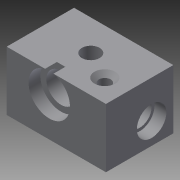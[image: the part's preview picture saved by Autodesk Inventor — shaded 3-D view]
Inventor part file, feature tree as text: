
AUTODESK INVENTOR PART (.ipt)
format: ipt  version: 2015 SP2 (Build 190223200, 223)  size: 123,904 bytes
history: native  units: mm
features: hole x4, sketch x2, extrude x1
ambient origin geometry x8: Origin, YZ Plane, XZ Plane, XY Plane, X Axis, Y Axis, Z Axis, Center Point
bodies: Volumenkörper1 (feature_tree)
feature tree (7):
  extrude  "Extrusion1"  Depth=10.0mm
  hole  "Drill01"  [1 undecoded]
  hole  "Drill02"  [1 undecoded]
  hole  "Drill03"  [1 undecoded]
  hole  "Drill04"  [1 undecoded]
  sketch  "Skizze1"  dims[d0=10.0mm d1=0.0mm]
  sketch  "Skizze2"  dims[d2=3.0mm d3=6.0mm d4=4.4mm d5=3.58mm d6=90.0deg d7=8.0mm d8=120.0deg d9=10.0mm d10=10.0mm d11=4.0mm d12=6.0mm d13=5.0mm d14=2.0mm d15=90.0deg d16=4.0mm d17=20.594885mm d18=10.0mm d19=10.0mm d20=5.0mm d21=6.0mm d22=7.0mm d23=2.0mm d24=90.0deg d25=4.0mm d26=20.594885mm d27=10.0mm d28=10.0mm d29=2.0mm d30=6.0mm d31=3.5mm d32=2.0mm d33=90.0deg d34=6.0mm d35=20.594885mm]
note: 4 required parameter values undecoded (feature->parameter linkage not recoverable at this tier; creation-order binding heuristic only, values carry confidence <= 0.55)
